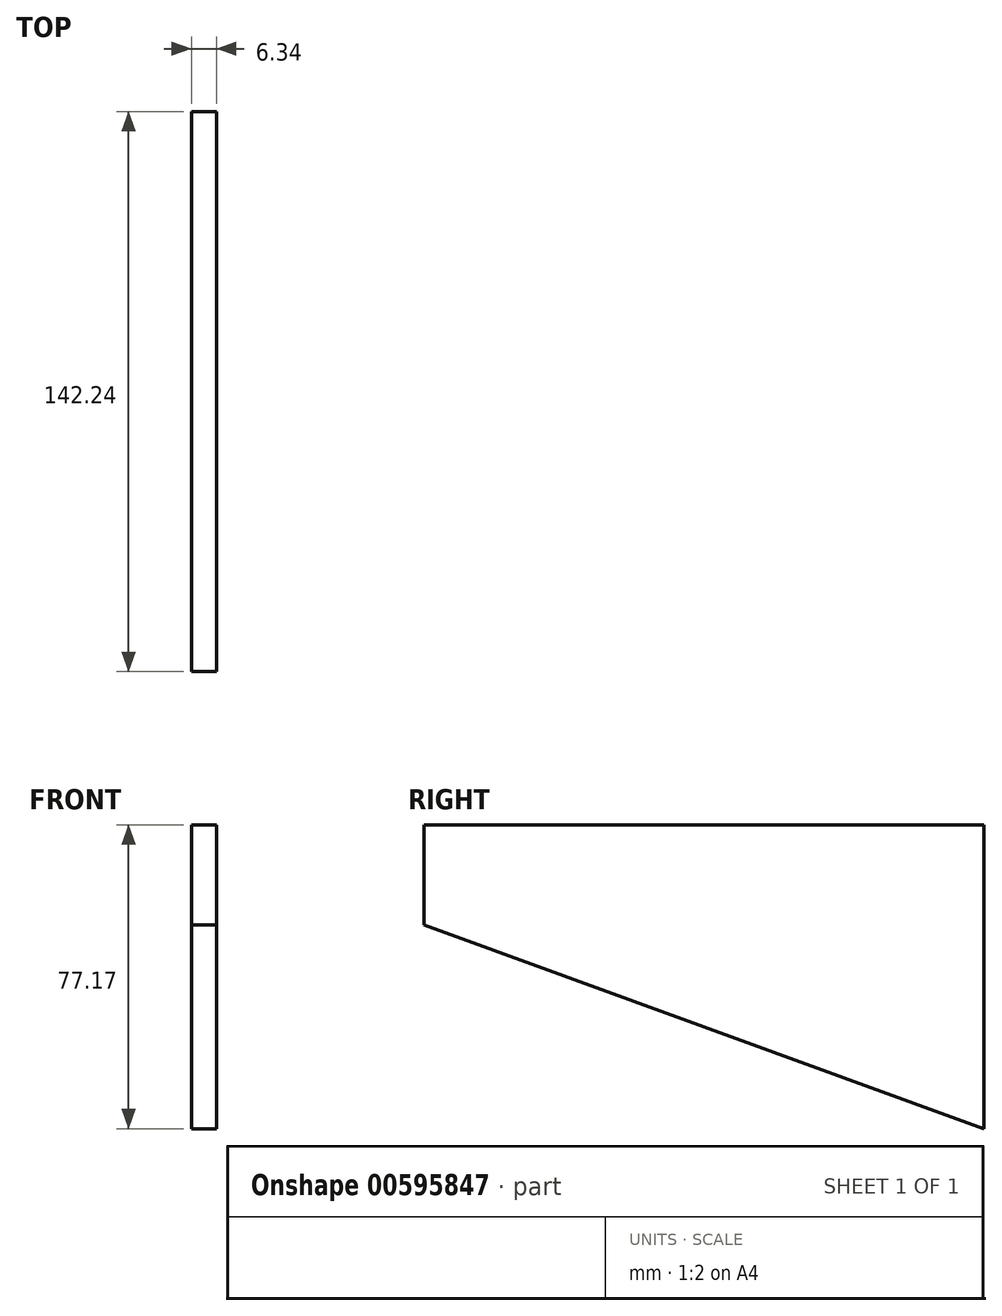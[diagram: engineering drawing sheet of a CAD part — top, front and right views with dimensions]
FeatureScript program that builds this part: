
annotation { "Feature Type Name" : "Feature", "Feature Type Description" : "" }
export const myFeature = defineFeature(function(context is Context, id is Id, definition is map)
    precondition{}
    {
        {
            var Q0;
            Q0=qCreatedBy(makeId("Right.planeOp"),FACE);
            var sketch = newSketch(context, id + "F0", { "sketchPlane" : qUnion([Q0])});
            skLineSegment(sketch, "E0", {"start": v(0, 0) * mm, "end": v(142.24, 0) * mm});
            skLineSegment(sketch, "E1", {"start": v(142.24, 0) * mm, "end": v(142.24, -77.17) * mm});
            skLineSegment(sketch, "E2", {"start": v(142.24, -77.17) * mm, "end": v(0, -25.4) * mm});
            skLineSegment(sketch, "E3", {"start": v(0, -25.4) * mm, "end": v(0, 0) * mm});
            skSolve(sketch);
        }
        {
            var Q0;
            Q0 = qSketchRegion(id + "F0", true);
            extrude(context, id + "F1", {"entities" : qUnion([Q0]), "endBound" : BoundingType.SYMMETRIC, "depth" : 6.35 * mm, "offsetDistance" : 25.4 * mm});
        }
    });
